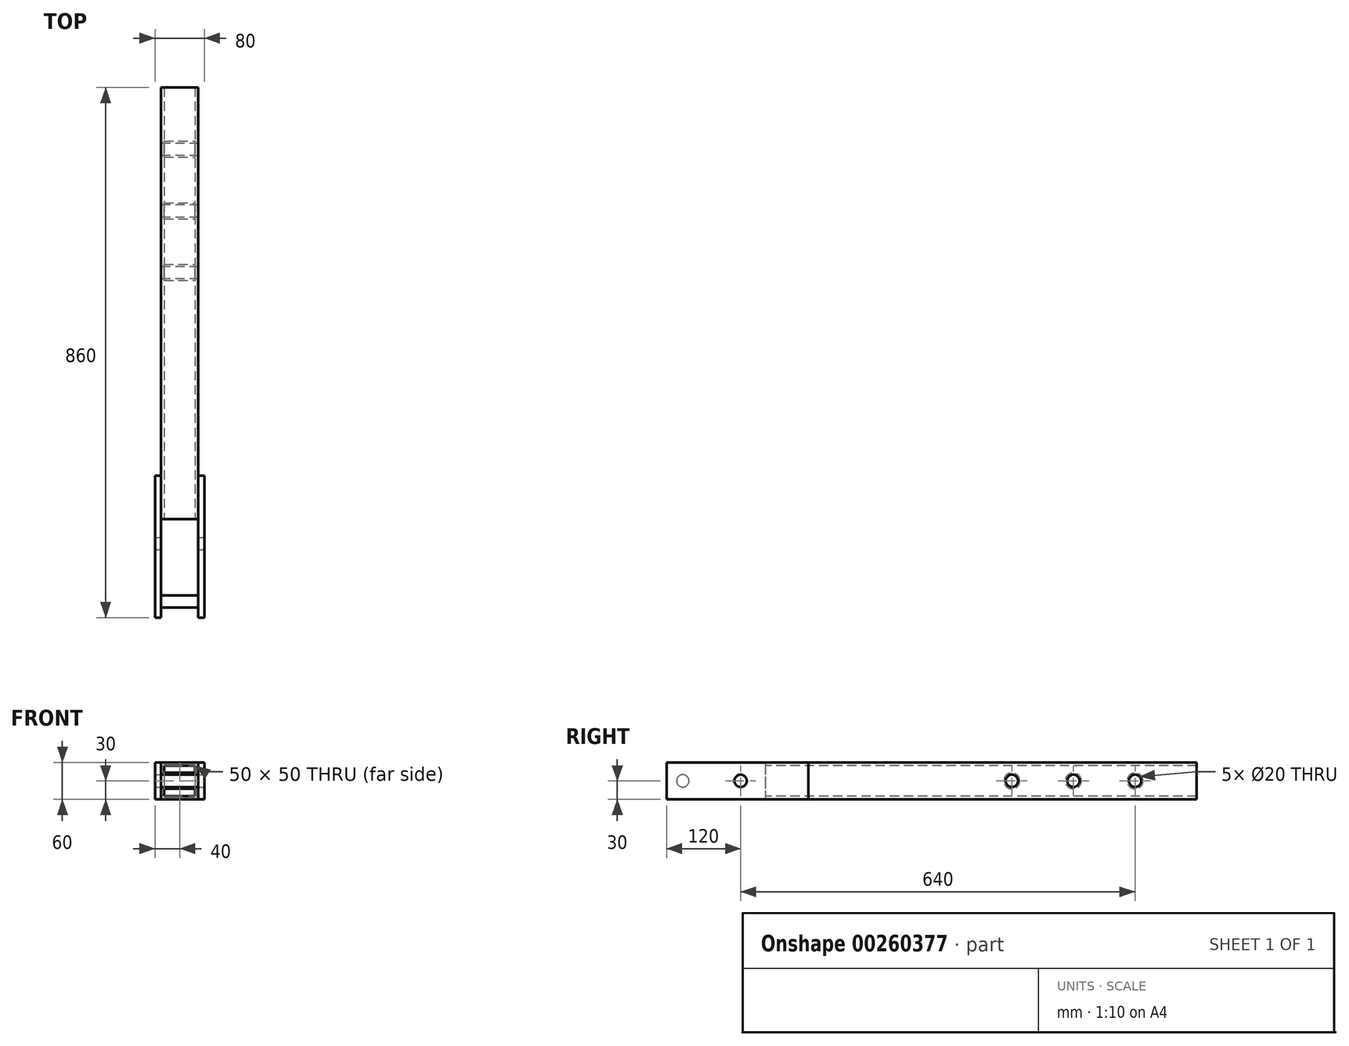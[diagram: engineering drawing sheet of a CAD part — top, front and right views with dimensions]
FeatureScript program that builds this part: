
annotation { "Feature Type Name" : "Feature", "Feature Type Description" : "" }
export const myFeature = defineFeature(function(context is Context, id is Id, definition is map)
    precondition{}
    {
        {
            var Q0;
            Q0=qCreatedBy(makeId("Front.planeOp"),FACE);
            var sketch = newSketch(context, id + "F0", { "sketchPlane" : qUnion([Q0])});
            skLineSegment(sketch, "E0.bottom", {"start": v(30, 30) * mm, "end": v(-30, 30) * mm});
            skLineSegment(sketch, "E0.top", {"start": v(30, -30) * mm, "end": v(-30, -30) * mm});
            skLineSegment(sketch, "E0.left", {"start": v(30, 30) * mm, "end": v(30, -30) * mm});
            skLineSegment(sketch, "E0.right", {"start": v(-30, 30) * mm, "end": v(-30, -30) * mm});
            skPoint(sketch, "E0.middle", {"position": v(0, 0) * mm});
            skLineSegment(sketch, "E1.bottom", {"start": v(25, 25) * mm, "end": v(-25, 25) * mm});
            skLineSegment(sketch, "E1.top", {"start": v(25, -25) * mm, "end": v(-25, -25) * mm});
            skLineSegment(sketch, "E1.left", {"start": v(25, 25) * mm, "end": v(25, -25) * mm});
            skLineSegment(sketch, "E1.right", {"start": v(-25, 25) * mm, "end": v(-25, -25) * mm});
            skSolve(sketch);
        }
        {
            var Q0;
            Q0 = qSketchRegion(id + "F0", true);
            extrude(context, id + "F1", {"entities" : qUnion([Q0]), "oppositeDirection" : true, "depth" : 700 * mm});
        }
        {
            var Q0;
            Q0=makeQuery(id+"F1.opExtrude","SWEPT_FACE",FACE,{"disambiguationData":[OSD([sQuery(id+"F0.wireOp",EDGE,"E0.left")])]});
            var sketch = newSketch(context, id + "F2", { "sketchPlane" : qUnion([Q0])});
            skLineSegment(sketch, "E2.bottom", {"start": v(70, 30) * mm, "end": v(-160, 30) * mm});
            skLineSegment(sketch, "E2.top", {"start": v(70, -30) * mm, "end": v(-160, -30) * mm});
            skLineSegment(sketch, "E2.left", {"start": v(70, 30) * mm, "end": v(70, -30) * mm});
            skLineSegment(sketch, "E2.right", {"start": v(-160, 30) * mm, "end": v(-160, -30) * mm});
            skSolve(sketch);
        }
        {
            var Q0;
            {var subQ2=sQuery(id+"F2.wireOp",EDGE,"E2.right");Q0=makeQuery(id+"F2.imprint","IMPRINT",FACE,{"disambiguationData":[TD([[makeQuery(id+"F2.imprint","IMPRINT",EDGE,{"derivedFrom":subQ2}),1.0]])]});}
            var Q1;
            {var subQ3=sQuery(id+"F2.wireOp",EDGE,"E2.left");Q1=makeQuery(id+"F2.imprint","IMPRINT",FACE,{"disambiguationData":[TD([[makeQuery(id+"F2.imprint","IMPRINT",EDGE,{"derivedFrom":subQ3}),-1.0]])]});}
            extrude(context, id + "F3", {"entities" : qUnion([Q0, Q1]), "depth" : 10 * mm});
        }
        {
            var Q0;
            Q0=makeQuery(id+"F3.opExtrude","CAP_FACE",FACE,{"disambiguationData":[OSD([sQuery(id+"F2.wireOp",EDGE,"E2.bottom"),sQuery(id+"F2.wireOp",EDGE,"E2.top"),sQuery(id+"F2.wireOp",EDGE,"E2.left"),sQuery(id+"F2.wireOp",EDGE,"E2.right")])],"isStart":false});
            var sketch = newSketch(context, id + "F4", { "sketchPlane" : qUnion([Q0])});
            skCircle(sketch, "E3", {"center": v(-133.81, 0) * mm, "radius": 10 * mm});
            skPoint(sketch, "E3.centerSnap0", {"position": v(-160, 0) * mm});
            skSolve(sketch);
        }
        {
            var Q0;
            Q0=makeQuery(id+"F3.opExtrude","SWEPT_BODY",BODY,{"disambiguationData":[OSD([sQuery(id+"F2.wireOp",EDGE,"E2.bottom"),sQuery(id+"F2.wireOp",EDGE,"E2.top"),sQuery(id+"F2.wireOp",EDGE,"E2.left"),sQuery(id+"F2.wireOp",EDGE,"E2.right")])]});
            var Q1;
            Q1=qCreatedBy(makeId("Right.planeOp"),FACE);
            mirror(context, id + "F5", {"entities" : qUnion([Q0]), "mirrorPlane" : qUnion([Q1])});
        }
        {
            var Q0;
            Q0=makeQuery(id+"F4.imprint","IMPRINT",FACE,{"disambiguationData":[TD([[makeQuery(id+"F4.imprint","IMPRINT",EDGE,{"derivedFrom":sQuery(id+"F4.wireOp",EDGE,"E3")}),1.0]])]});
            var Q1;
            Q1=makeQuery(id+"F5.opPattern","COPY",FACE,{"derivedFrom":makeQuery(id+"F3.opExtrude","CAP_FACE",FACE,{"disambiguationData":[OSD([sQuery(id+"F2.wireOp",EDGE,"E2.bottom"),sQuery(id+"F2.wireOp",EDGE,"E2.top"),sQuery(id+"F2.wireOp",EDGE,"E2.left"),sQuery(id+"F2.wireOp",EDGE,"E2.right")])],"isStart":true}),"instanceName":"1"});
            extrude(context, id + "F6", {"entities" : qUnion([Q0]), "operationType" : NewBodyOperationType.ADD, "endBound" : BoundingType.UP_TO_SURFACE, "oppositeDirection" : true, "endBoundEntityFace" : qUnion([Q1]), "depth" : 25 * mm});
        }
        {
            var Q0;
            Q0=makeQuery(id+"F1.opExtrude","SWEPT_FACE",FACE,{"disambiguationData":[OSD([sQuery(id+"F0.wireOp",EDGE,"E0.left")])]});
            var sketch = newSketch(context, id + "F7", { "sketchPlane" : qUnion([Q0])});
            skCircle(sketch, "E4", {"center": v(600, 0) * mm, "radius": 10 * mm});
            skPoint(sketch, "E4.centerSnap0", {"position": v(700, 0) * mm});
            skCircle(sketch, "E5", {"center": v(500, 0) * mm, "radius": 10 * mm});
            skCircle(sketch, "E6", {"center": v(400, 0) * mm, "radius": 10 * mm});
            skCircle(sketch, "E7", {"center": v(400, 0) * mm, "radius": 13 * mm});
            skCircle(sketch, "E8", {"center": v(500, 0) * mm, "radius": 13 * mm});
            skCircle(sketch, "E9", {"center": v(600, 0) * mm, "radius": 13 * mm});
            skSolve(sketch);
        }
        {
            var Q0;
            Q0 = qSketchRegion(id + "F7", true);
            var Q1;
            Q1=makeQuery(id+"F1.opExtrude","SWEPT_FACE",FACE,{"disambiguationData":[OSD([sQuery(id+"F0.wireOp",EDGE,"E0.right")])]});
            extrude(context, id + "F8", {"entities" : qUnion([Q0]), "operationType" : NewBodyOperationType.ADD, "endBound" : BoundingType.UP_TO_SURFACE, "oppositeDirection" : true, "endBoundEntityFace" : qUnion([Q1]), "depth" : 25 * mm});
        }
        {
            var Q0;
            Q0=makeQuery(id+"F7.imprint","IMPRINT",FACE,{"disambiguationData":[TD([[makeQuery(id+"F7.imprint","IMPRINT",EDGE,{"derivedFrom":sQuery(id+"F7.wireOp",EDGE,"E4")}),1.0]])]});
            var Q1;
            Q1=makeQuery(id+"F7.imprint","IMPRINT",FACE,{"disambiguationData":[TD([[makeQuery(id+"F7.imprint","IMPRINT",EDGE,{"derivedFrom":sQuery(id+"F7.wireOp",EDGE,"E5")}),1.0]])]});
            var Q2;
            Q2=makeQuery(id+"F7.imprint","IMPRINT",FACE,{"disambiguationData":[TD([[makeQuery(id+"F7.imprint","IMPRINT",EDGE,{"derivedFrom":sQuery(id+"F7.wireOp",EDGE,"E6")}),1.0]])]});
            extrude(context, id + "F9", {"entities" : qUnion([Q0, Q1, Q2]), "operationType" : NewBodyOperationType.REMOVE, "endBound" : BoundingType.THROUGH_ALL, "oppositeDirection" : true, "depth" : 25 * mm});
        }
        {
            var Q0;
            Q0=makeQuery(id+"F3.opExtrude","CAP_FACE",FACE,{"disambiguationData":[OSD([sQuery(id+"F2.wireOp",EDGE,"E2.bottom"),sQuery(id+"F2.wireOp",EDGE,"E2.top"),sQuery(id+"F2.wireOp",EDGE,"E2.left"),sQuery(id+"F2.wireOp",EDGE,"E2.right")])],"isStart":false});
            var sketch = newSketch(context, id + "F10", { "sketchPlane" : qUnion([Q0])});
            skCircle(sketch, "E10", {"center": v(-40, 0) * mm, "radius": 10 * mm});
            skPoint(sketch, "E10.centerSnap0", {"position": v(-160, 0) * mm});
            skSolve(sketch);
        }
        {
            var Q0;
            Q0=makeQuery(id+"F10.imprint","IMPRINT",FACE,{"disambiguationData":[TD([[makeQuery(id+"F10.imprint","IMPRINT",EDGE,{"derivedFrom":sQuery(id+"F10.wireOp",EDGE,"E10")}),1.0]])]});
            var Q1;
            Q1=makeQuery(id+"F3.opExtrude","CAP_FACE",FACE,{"disambiguationData":[OSD([sQuery(id+"F2.wireOp",EDGE,"E2.bottom"),sQuery(id+"F2.wireOp",EDGE,"E2.top"),sQuery(id+"F2.wireOp",EDGE,"E2.left"),sQuery(id+"F2.wireOp",EDGE,"E2.right")])],"isStart":false});
            extrude(context, id + "F11", {"entities" : qUnion([Q0]), "operationType" : NewBodyOperationType.REMOVE, "endBound" : BoundingType.THROUGH_ALL, "oppositeDirection" : true, "endBoundEntityFace" : qUnion([Q1]), "depth" : 25 * mm});
        }
    });
